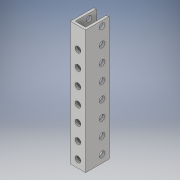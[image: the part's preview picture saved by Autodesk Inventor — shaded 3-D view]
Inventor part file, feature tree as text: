
AUTODESK INVENTOR PART (.ipt)
format: ipt  version: 2017 (Build 210142000, 142)  size: 171,520 bytes
history: native  units: in
note: dims shown in document units (in); Inventor stores cm internally (conversion verified against a paired STEP export)
features: direct_edit x1, hole x1, sketch x1, fillet x1, move_body x1
ambient origin geometry x8: Origin, YZ Plane, XZ Plane, XY Plane, X Axis, Y Axis, Z Axis, Center Point
bodies: Solid1 (feature_tree)
feature tree (5):
  direct_edit  "Direct Edit1"
  hole  "Hole1"  [1 undecoded]
  sketch  "Sketch1"  dims[d0=0.0in d1=0.0in d2=0.315in d3=0.385in d4=0.385in d5=0.14in d6=0.75in d7=0.375in d8=0.25in d9=0.5635in d10=1.0in d11=0.8108in]
  fillet  "Fillet1"  Radius=0.385in
  move_body  "Move1"
note: 1 required parameter value undecoded (feature->parameter linkage not recoverable at this tier; creation-order binding heuristic only, values carry confidence <= 0.55)
